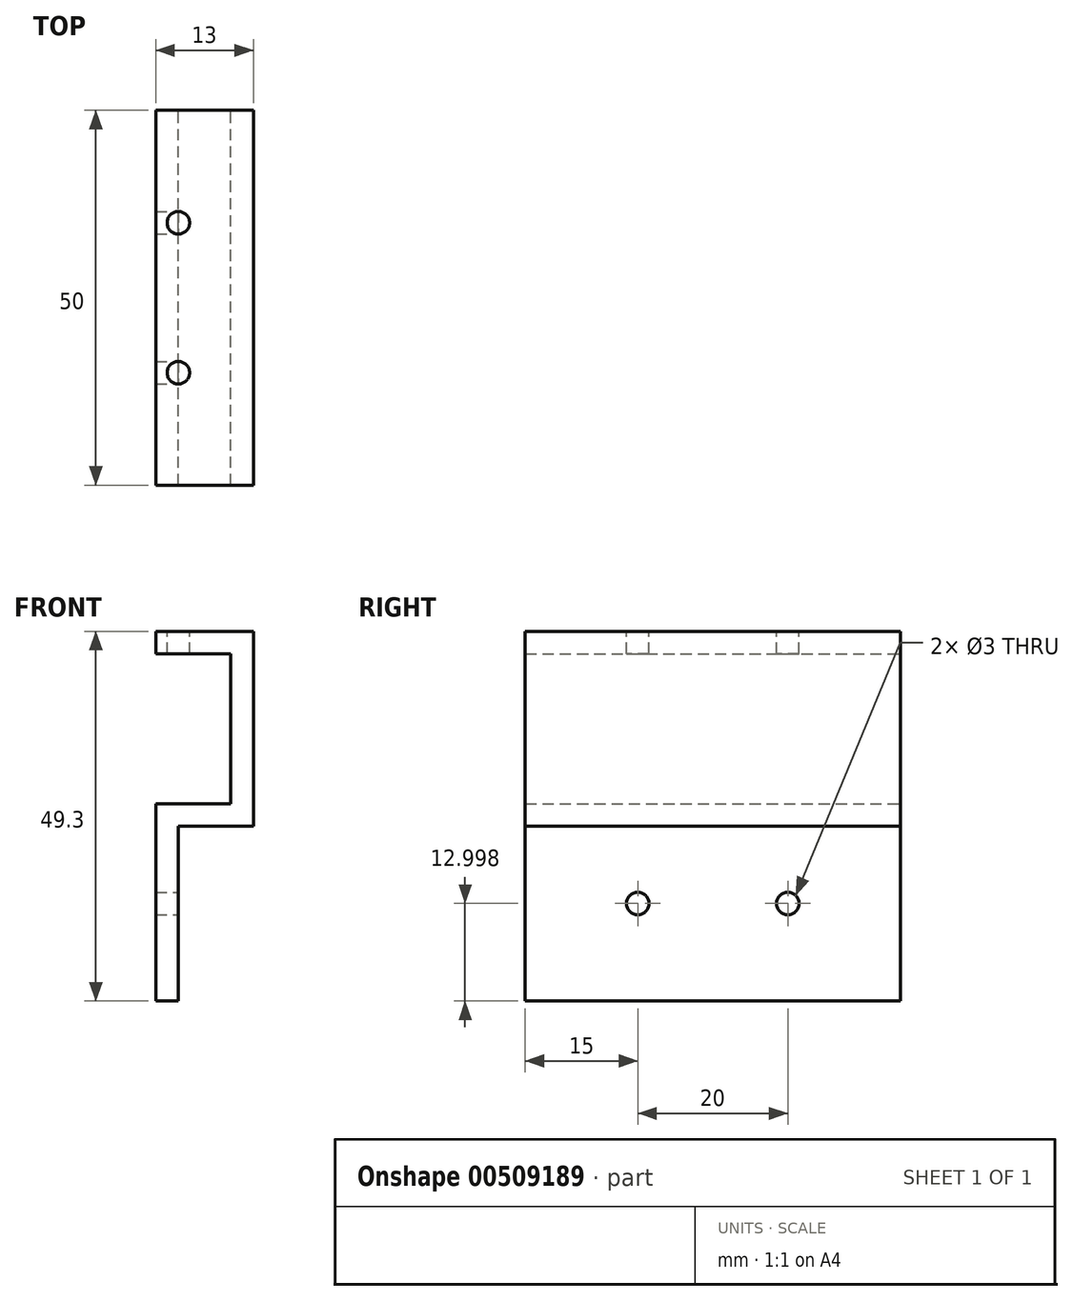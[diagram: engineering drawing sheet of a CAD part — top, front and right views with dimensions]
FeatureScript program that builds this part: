
annotation { "Feature Type Name" : "Feature", "Feature Type Description" : "" }
export const myFeature = defineFeature(function(context is Context, id is Id, definition is map)
    precondition{}
    {
        {
            var Q0;
            Q0=qCreatedBy(makeId("Front.planeOp"),FACE);
            var sketch = newSketch(context, id + "F0", { "sketchPlane" : qUnion([Q0])});
            skLineSegment(sketch, "E0", {"start": v(-9.26, 39.4) * mm, "end": v(0.74, 39.4) * mm});
            skLineSegment(sketch, "E1", {"start": v(0.74, 39.4) * mm, "end": v(0.74, 19.4) * mm});
            skLineSegment(sketch, "E2", {"start": v(0.74, 19.4) * mm, "end": v(-9.26, 19.4) * mm});
            skLineSegment(sketch, "E3", {"start": v(-9.26, 19.4) * mm, "end": v(-9.26, -6.9) * mm});
            skLineSegment(sketch, "E4.0", {"start": v(-6.26, 16.4) * mm, "end": v(-6.26, -6.9) * mm});
            skLineSegment(sketch, "E4.1", {"start": v(3.74, 16.4) * mm, "end": v(-6.26, 16.4) * mm});
            skLineSegment(sketch, "E4.2", {"start": v(3.74, 42.4) * mm, "end": v(3.74, 16.4) * mm});
            skLineSegment(sketch, "E4.3", {"start": v(-9.26, 42.4) * mm, "end": v(3.74, 42.4) * mm});
            skLineSegment(sketch, "E5", {"start": v(-9.26, 42.4) * mm, "end": v(-9.26, 39.4) * mm});
            skLineSegment(sketch, "E6", {"start": v(-9.26, -6.9) * mm, "end": v(-6.26, -6.9) * mm});
            skSolve(sketch);
        }
        {
            var Q0;
            Q0 = qSketchRegion(id + "F0", true);
            extrude(context, id + "F1", {"entities" : qUnion([Q0]), "depth" : 50 * mm});
        }
        {
            var Q0;
            Q0=makeQuery(id+"F1.opExtrude","SWEPT_FACE",FACE,{"disambiguationData":[OSD([sQuery(id+"F0.wireOp",EDGE,"E4.3")])]});
            var sketch = newSketch(context, id + "F2", { "sketchPlane" : qUnion([Q0])});
            skCircle(sketch, "E7", {"center": v(-6.26, -35) * mm, "radius": 1.5 * mm});
            skLineSegment(sketch, "E8", {"start": v(-6.26, -35) * mm, "end": v(-6.26, -6.62) * mm, "construction": true});
            skCircle(sketch, "E9", {"center": v(-6.26, -15) * mm, "radius": 1.5 * mm});
            skSolve(sketch);
        }
        {
            var Q0;
            Q0 = qSketchRegion(id + "F2", true);
            extrude(context, id + "F3", {"entities" : qUnion([Q0]), "operationType" : NewBodyOperationType.REMOVE, "oppositeDirection" : true, "depth" : 10 * mm});
        }
        {
            var Q0;
            Q0=makeQuery(id+"F1.opExtrude","SWEPT_FACE",FACE,{"disambiguationData":[OSD([sQuery(id+"F0.wireOp",EDGE,"E4.0")])]});
            var sketch = newSketch(context, id + "F4", { "sketchPlane" : qUnion([Q0])});
            skLineSegment(sketch, "E10", {"start": v(-59.92, 6.1) * mm, "end": v(17.83, 6.1) * mm, "construction": true});
            skCircle(sketch, "E11", {"center": v(-35, 6.1) * mm, "radius": 1.5 * mm});
            skCircle(sketch, "E12", {"center": v(-15, 6.1) * mm, "radius": 1.5 * mm});
            skSolve(sketch);
        }
        {
            var Q0;
            Q0 = qSketchRegion(id + "F4", true);
            extrude(context, id + "F5", {"entities" : qUnion([Q0]), "operationType" : NewBodyOperationType.REMOVE, "oppositeDirection" : true, "depth" : 25 * mm});
        }
    });
